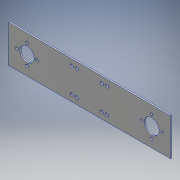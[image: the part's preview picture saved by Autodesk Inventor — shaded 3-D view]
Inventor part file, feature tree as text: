
AUTODESK INVENTOR PART (.ipt)
format: ipt  version: 2016 (Build 200138000, 138)  size: 174,592 bytes
history: native  units: mm
features: extrude x6, sketch x6, other x1
ambient origin geometry x8: Origin, YZ Plane, XZ Plane, XY Plane, X Axis, Y Axis, Z Axis, Center Point
bodies: Body1 (feature_tree)
feature tree (13):
  other  "ソリッド1"
  extrude  "押し出し1"  Depth=260.0mm
  extrude  "押し出し2"  Depth=60.0mm
  extrude  "押し出し3"  Depth=2.0mm TaperAngle=0.0deg
  extrude  "押し出し4"  Depth=24.0mm
  extrude  "押し出し6"  Depth=30.0mm
  extrude  "押し出し7"  Depth=30.0mm
  sketch  "スケッチ1"
  sketch  "スケッチ2"
  sketch  "スケッチ3"
  sketch  "スケッチ4"
  sketch  "スケッチ5"
  sketch  "スケッチ6"
